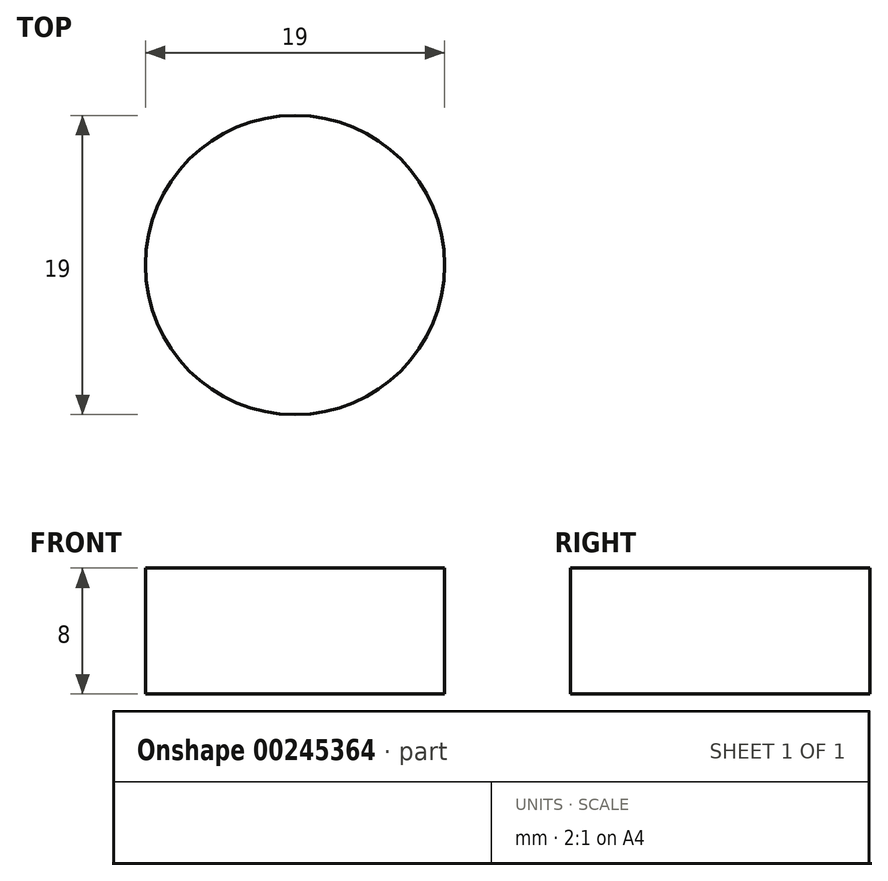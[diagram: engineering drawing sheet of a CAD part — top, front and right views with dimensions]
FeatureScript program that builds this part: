
annotation { "Feature Type Name" : "Feature", "Feature Type Description" : "" }
export const myFeature = defineFeature(function(context is Context, id is Id, definition is map)
    precondition{}
    {
        {
            var Q0;
            Q0=qCreatedBy(makeId("Top.planeOp"),FACE);
            var sketch = newSketch(context, id + "F0", { "sketchPlane" : qUnion([Q0])});
            skCircle(sketch, "E0", {"center": v(0, 0) * mm, "radius": 9.5 * mm});
            skSolve(sketch);
        }
        {
            var Q0;
            Q0=makeQuery(id+"F0.imprint","IMPRINT",FACE,{"disambiguationData":[TD([[makeQuery(id+"F0.imprint","IMPRINT",EDGE,{"derivedFrom":sQuery(id+"F0.wireOp",EDGE,"E0")}),1.0]])]});
            extrude(context, id + "F1", {"entities" : qUnion([Q0]), "depth" : 8 * mm});
        }
    });
